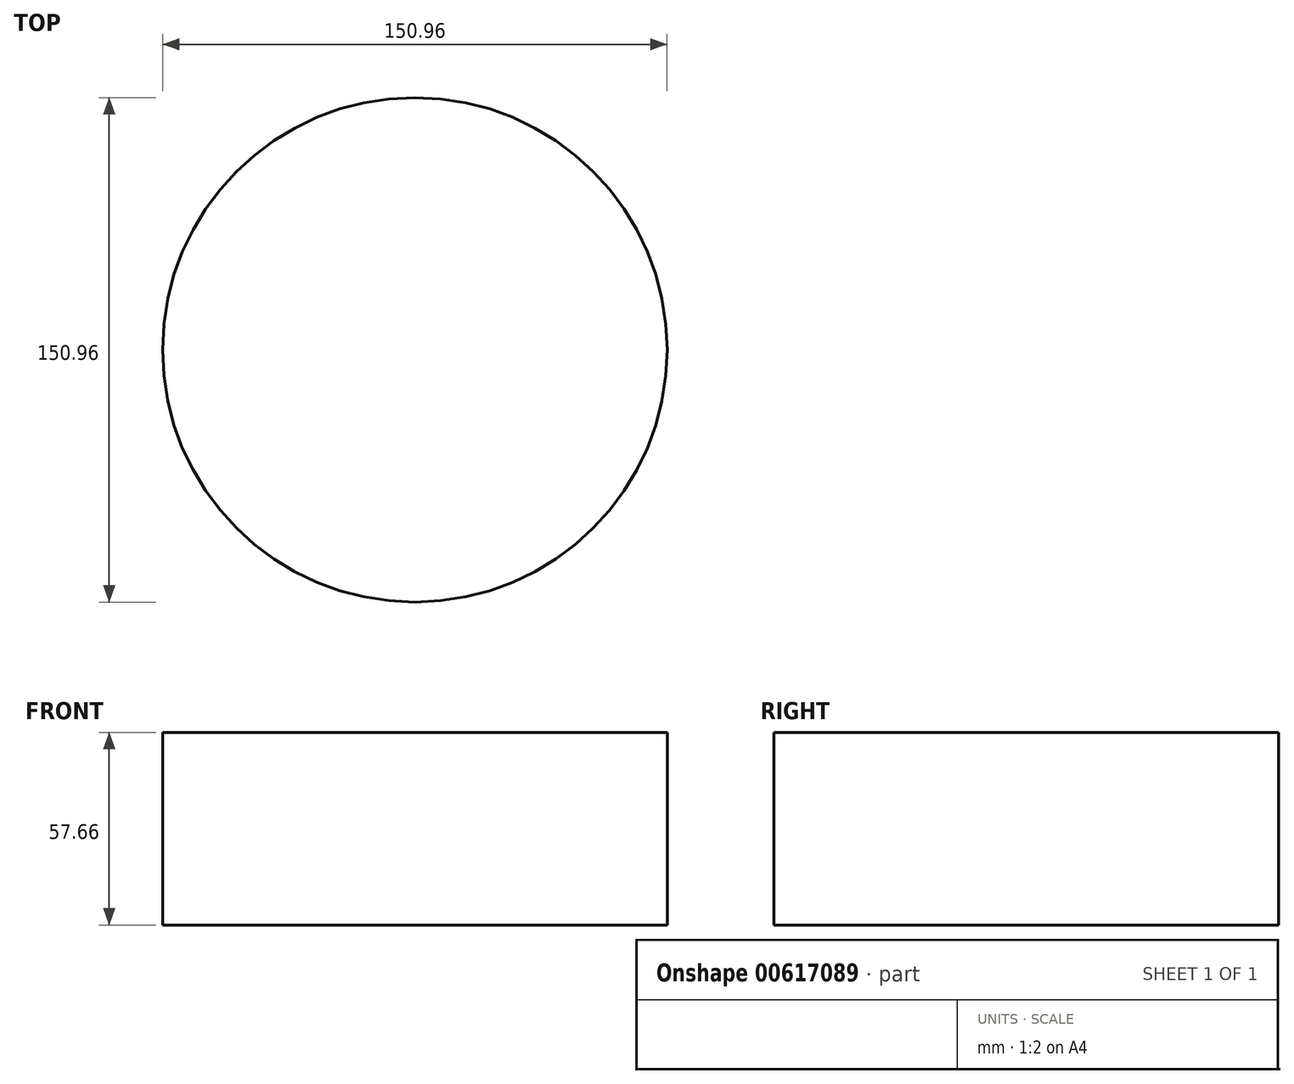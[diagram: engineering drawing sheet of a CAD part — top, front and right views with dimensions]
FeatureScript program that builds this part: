
annotation { "Feature Type Name" : "Feature", "Feature Type Description" : "" }
export const myFeature = defineFeature(function(context is Context, id is Id, definition is map)
    precondition{}
    {
        {
            var Q0;
            Q0=qCreatedBy(makeId("Top.planeOp"),FACE);
            var sketch = newSketch(context, id + "F0", { "sketchPlane" : qUnion([Q0])});
            skCircle(sketch, "E0", {"center": v(0, 0) * mm, "radius": 75.48 * mm});
            skSolve(sketch);
        }
        {
            var Q0;
            Q0=makeQuery(id+"F0.imprint","IMPRINT",FACE,{"disambiguationData":[TD([[makeQuery(id+"F0.imprint","IMPRINT",EDGE,{"derivedFrom":sQuery(id+"F0.wireOp",EDGE,"E0")}),1.0]])]});
            extrude(context, id + "F1", {"entities" : qUnion([Q0]), "depth" : 57.66 * mm, "offsetDistance" : 25.4 * mm});
        }
    });
